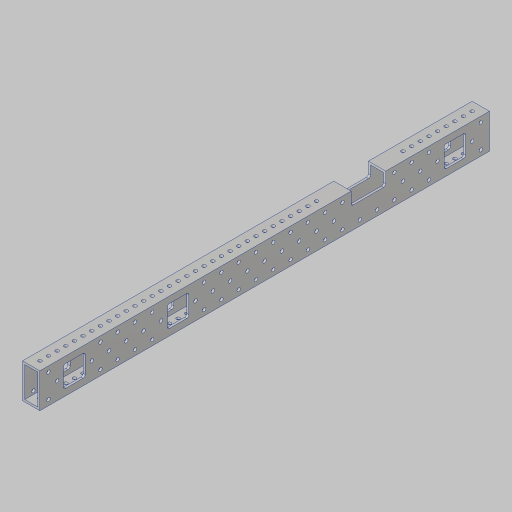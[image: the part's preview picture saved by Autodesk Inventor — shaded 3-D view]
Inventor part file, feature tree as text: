
AUTODESK INVENTOR PART (.ipt)
format: ipt  version: 2023.5 (Build 275446000, 446)  size: 451,584 bytes
history: native  units: in
note: dims shown in document units (in); Inventor stores cm internally (conversion verified against a paired STEP export)
features: sketch x4, extrude x3, hole x2, fillet x2, projected_geometry x1
ambient origin geometry x8: Origin, YZ Plane, XZ Plane, XY Plane, X Axis, Y Axis, Z Axis, Center Point
bodies: Solid1 (feature_tree)
feature tree (12):
  extrude  "Extrusion1"  Depth=1.0in
  hole  "Hole1"  [1 undecoded]
  hole  "Hole2"  [1 undecoded]
  extrude  "Extrusion3"  Depth=0.375in
  fillet  "Fillet1"  Radius=1.0in
  extrude  "Extrusion4"  Depth=1.0in
  fillet  "Fillet2"  Radius=1.0in
  sketch  "Sketch2"  dims[d4=0.0in d6=1.0in]
  sketch  "Sketch3"  dims[d7=9.8425in d9=0.5in d10=0.3937in d12=1.0in d14=9.8425in d16=0.5in d17=0.3937in d19=1.0in]
  sketch  "Sketch5"  dims[d21=0.201in d22=0.75in d23=0.385in d24=0.25in d25=0.5635in d26=1.0in d27=0.8108in d28=0.5in]
  sketch  "Sketch6"  dims[d29=0.375in d30=0.375in d31=1.0in d32=5.1181in d34=1.0in d35=0.3937in d37=1.0in d39=5.1181in d41=1.0in d42=0.3937in d44=1.0in d46=0.201in d47=0.75in d48=0.375in d49=0.25in d50=0.5635in d51=1.0in d52=0.8108in d59=1.25in d60=1.25in d61=1.0in d62=0.0in d63=0.125in d64=6.0in d66=0.75in d67=2.0in d69=1.0in d70=0.0in d71=0.125in d72=0.0in d73=0.0in d74=0.0in d75=0.0in]
  projected_geometry  "Project Cut Edges1"
note: 2 required parameter values undecoded (feature->parameter linkage not recoverable at this tier; creation-order binding heuristic only, values carry confidence <= 0.55)
